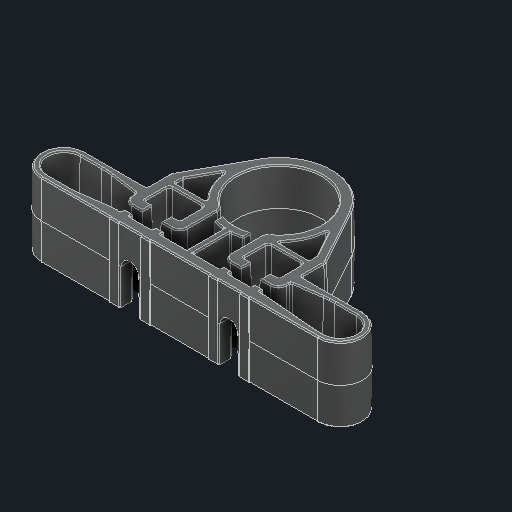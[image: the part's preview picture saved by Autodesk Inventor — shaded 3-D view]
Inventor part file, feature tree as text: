
AUTODESK INVENTOR PART (.ipt)
format: ipt  version: 2024.2 (Build 282272000, 272)  size: 1,220,096 bytes
history: native  units: in
note: dims shown in document units (in); Inventor stores cm internally (conversion verified against a paired STEP export)
features: fillet x1
ambient origin geometry x8: Origin, YZ Plane, XZ Plane, XY Plane, X Axis, Y Axis, Z Axis, Center Point
bodies: Solid1 (feature_tree)
feature tree (1):
  fillet  "Fillet26"  [1 undecoded]
note: 1 required parameter value undecoded (feature->parameter linkage not recoverable at this tier; creation-order binding heuristic only, values carry confidence <= 0.55)
